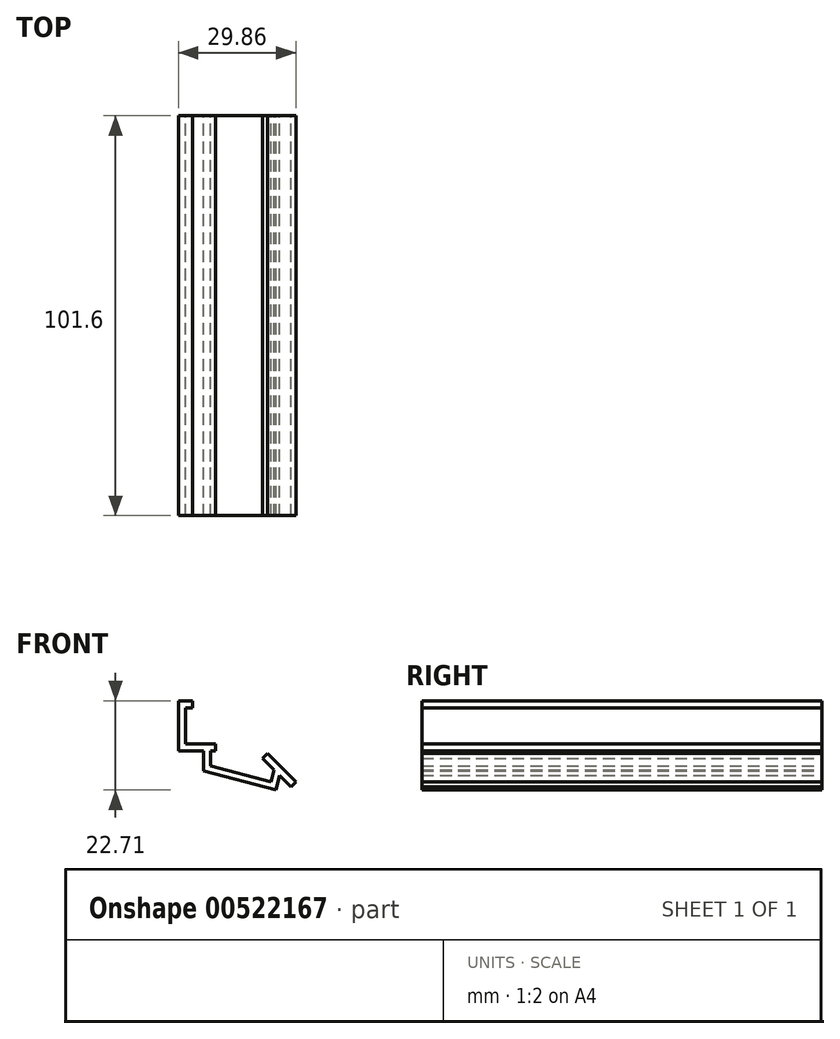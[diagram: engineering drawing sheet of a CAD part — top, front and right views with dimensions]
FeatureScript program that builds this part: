
annotation { "Feature Type Name" : "Feature", "Feature Type Description" : "" }
export const myFeature = defineFeature(function(context is Context, id is Id, definition is map)
    precondition{}
    {
        {
            var Q0;
            Q0=qCreatedBy(makeId("Front.planeOp"),FACE);
            var sketch = newSketch(context, id + "F0", { "sketchPlane" : qUnion([Q0])});
            skLineSegment(sketch, "E0", {"start": v(0, 17.78) * mm, "end": v(0, 5.08) * mm});
            skLineSegment(sketch, "E1", {"start": v(0, 5.08) * mm, "end": v(6.35, 5.08) * mm});
            skLineSegment(sketch, "E2", {"start": v(6.35, 5.08) * mm, "end": v(6.35, 0) * mm});
            skLineSegment(sketch, "E3", {"start": v(6.35, 0) * mm, "end": v(24.75, -4.93) * mm});
            skLineSegment(sketch, "E4", {"start": v(0, 17.78) * mm, "end": v(3.56, 17.78) * mm});
            skLineSegment(sketch, "E5", {"start": v(3.56, 17.78) * mm, "end": v(3.56, 16) * mm});
            skLineSegment(sketch, "E6", {"start": v(3.56, 16) * mm, "end": v(1.78, 16) * mm});
            skLineSegment(sketch, "E7", {"start": v(1.78, 16) * mm, "end": v(1.78, 6.86) * mm});
            skLineSegment(sketch, "E8", {"start": v(1.78, 6.86) * mm, "end": v(9.4, 6.86) * mm});
            skLineSegment(sketch, "E9", {"start": v(9.4, 6.86) * mm, "end": v(9.4, 5.08) * mm});
            skLineSegment(sketch, "E10", {"start": v(9.4, 5.08) * mm, "end": v(8.13, 5.08) * mm});
            skLineSegment(sketch, "E11", {"start": v(8.13, 5.08) * mm, "end": v(8.13, 1.27) * mm});
            skLineSegment(sketch, "E12", {"start": v(8.13, 1.27) * mm, "end": v(23.47, -2.84) * mm});
            skLineSegment(sketch, "E13", {"start": v(24.75, -4.93) * mm, "end": v(25.74, -1.25) * mm});
            skLineSegment(sketch, "E14", {"start": v(23.47, -2.84) * mm, "end": v(24.29, 0.2) * mm});
            skLineSegment(sketch, "E15", {"start": v(24.29, 0.2) * mm, "end": v(21.42, 3.07) * mm});
            skLineSegment(sketch, "E16", {"start": v(21.42, 3.07) * mm, "end": v(22.68, 4.32) * mm});
            skLineSegment(sketch, "E17", {"start": v(22.68, 4.32) * mm, "end": v(29.86, -2.86) * mm});
            skLineSegment(sketch, "E18", {"start": v(29.86, -2.86) * mm, "end": v(28.6, -4.12) * mm});
            skLineSegment(sketch, "E19", {"start": v(28.6, -4.12) * mm, "end": v(25.74, -1.25) * mm});
            skSolve(sketch);
        }
        {
            var Q0;
            Q0 = qSketchRegion(id + "F0", true);
            extrude(context, id + "F1", {"entities" : qUnion([Q0]), "depth" : 101.6 * mm, "offsetDistance" : 25.4 * mm});
        }
    });
